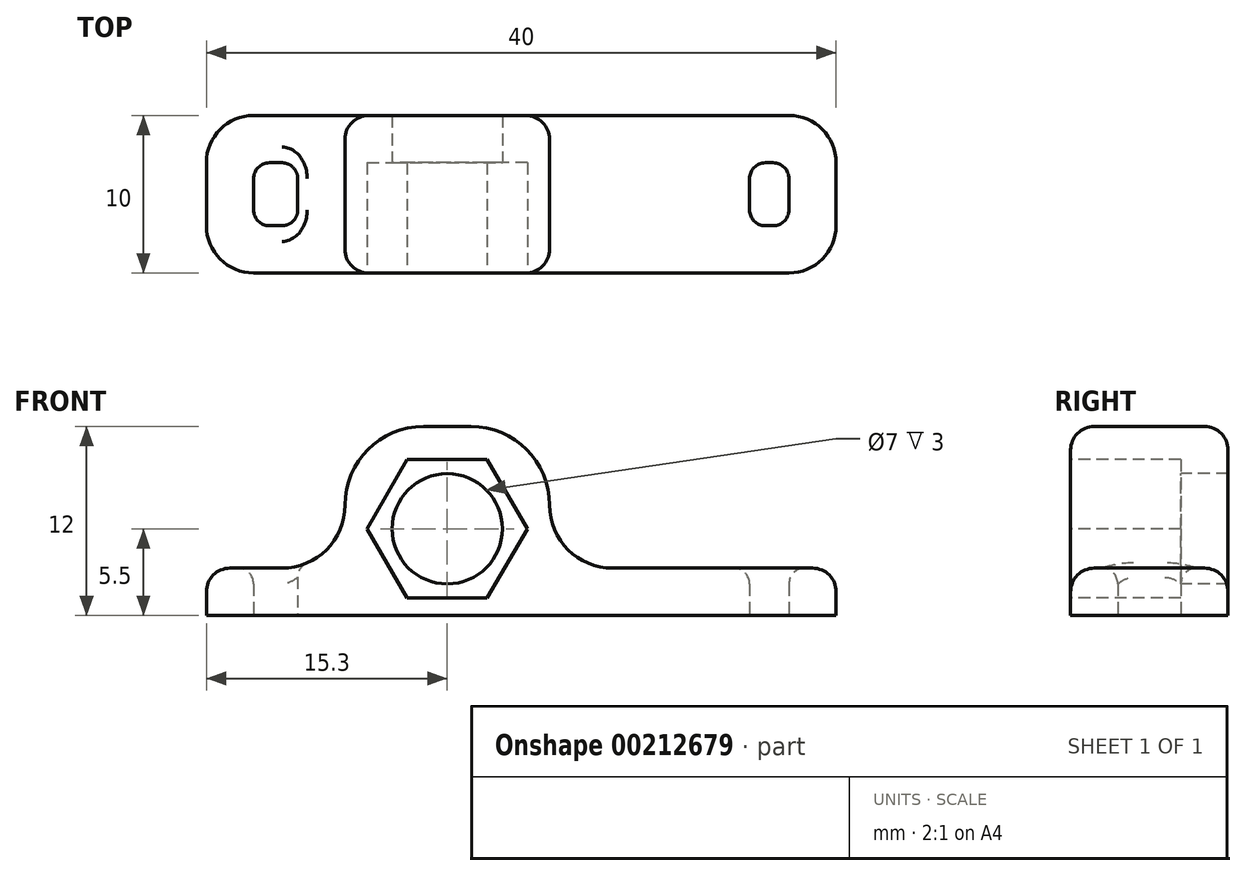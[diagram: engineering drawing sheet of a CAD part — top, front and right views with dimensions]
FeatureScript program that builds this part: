
annotation { "Feature Type Name" : "Feature", "Feature Type Description" : "" }
export const myFeature = defineFeature(function(context is Context, id is Id, definition is map)
    precondition{}
    {
        {
            var Q0;
            Q0=qCreatedBy(makeId("Top.planeOp"),FACE);
            var sketch = newSketch(context, id + "F0", { "sketchPlane" : qUnion([Q0])});
            skLineSegment(sketch, "E0.bottom", {"start": v(-17, 5) * mm, "end": v(17, 5) * mm});
            skLineSegment(sketch, "E0.top", {"start": v(-17, -5) * mm, "end": v(17, -5) * mm});
            skLineSegment(sketch, "E0.left", {"start": v(-20, 2) * mm, "end": v(-20, -2) * mm});
            skLineSegment(sketch, "E0.right", {"start": v(20, 2) * mm, "end": v(20, -2) * mm});
            skLineSegment(sketch, "E1.bottom", {"start": v(-16, 2) * mm, "end": v(-15.2, 2) * mm});
            skLineSegment(sketch, "E1.top", {"start": v(-16, -2) * mm, "end": v(-15.2, -2) * mm});
            skLineSegment(sketch, "E1.left", {"start": v(-17, 1) * mm, "end": v(-17, -1) * mm});
            skLineSegment(sketch, "E1.right", {"start": v(-14.2, 1) * mm, "end": v(-14.2, -1) * mm});
            skLineSegment(sketch, "E2.bottom", {"start": v(15.5, 2) * mm, "end": v(16, 2) * mm});
            skLineSegment(sketch, "E2.top", {"start": v(15.5, -2) * mm, "end": v(16, -2) * mm});
            skLineSegment(sketch, "E2.left", {"start": v(17, 1) * mm, "end": v(17, -1) * mm});
            skLineSegment(sketch, "E2.right", {"start": v(14.5, 1) * mm, "end": v(14.5, -1) * mm});
            skPoint(sketch, "E3.visualSharp", {"position": v(-17, 2) * mm});
            skArc(sketch, "E3.filletArc", {"start": v(-16, 2) * mm, "mid": v(-16.7, 1.7) * mm, "end": v(-17, 1) * mm});
            skPoint(sketch, "E4.visualSharp", {"position": v(-14.2, 2) * mm});
            skArc(sketch, "E4.filletArc", {"start": v(-14.2, 1) * mm, "mid": v(-14.5, 1.7) * mm, "end": v(-15.2, 2) * mm});
            skPoint(sketch, "E5.visualSharp", {"position": v(-17, -2) * mm});
            skArc(sketch, "E5.filletArc", {"start": v(-17, -1) * mm, "mid": v(-16.7, -1.7) * mm, "end": v(-16, -2) * mm});
            skPoint(sketch, "E6.visualSharp", {"position": v(-14.2, -2) * mm});
            skArc(sketch, "E6.filletArc", {"start": v(-15.2, -2) * mm, "mid": v(-14.5, -1.7) * mm, "end": v(-14.2, -1) * mm});
            skPoint(sketch, "E7.visualSharp", {"position": v(17, 2) * mm});
            skArc(sketch, "E7.filletArc", {"start": v(17, 1) * mm, "mid": v(16.7, 1.7) * mm, "end": v(16, 2) * mm});
            skPoint(sketch, "E8.visualSharp", {"position": v(14.5, 2) * mm});
            skArc(sketch, "E8.filletArc", {"start": v(15.5, 2) * mm, "mid": v(14.8, 1.7) * mm, "end": v(14.5, 1) * mm});
            skPoint(sketch, "E9.visualSharp", {"position": v(14.5, -2) * mm});
            skArc(sketch, "E9.filletArc", {"start": v(14.5, -1) * mm, "mid": v(14.8, -1.7) * mm, "end": v(15.5, -2) * mm});
            skPoint(sketch, "E10.visualSharp", {"position": v(17, -2) * mm});
            skArc(sketch, "E10.filletArc", {"start": v(16, -2) * mm, "mid": v(16.7, -1.7) * mm, "end": v(17, -1) * mm});
            skPoint(sketch, "E11.visualSharp", {"position": v(-20, 5) * mm});
            skArc(sketch, "E11.filletArc", {"start": v(-17, 5) * mm, "mid": v(-19.12, 4.12) * mm, "end": v(-20, 2) * mm});
            skPoint(sketch, "E12.visualSharp", {"position": v(-20, -5) * mm});
            skArc(sketch, "E12.filletArc", {"start": v(-20, -2) * mm, "mid": v(-19.12, -4.12) * mm, "end": v(-17, -5) * mm});
            skPoint(sketch, "E13.visualSharp", {"position": v(20, -5) * mm});
            skArc(sketch, "E13.filletArc", {"start": v(17, -5) * mm, "mid": v(19.12, -4.12) * mm, "end": v(20, -2) * mm});
            skPoint(sketch, "E14.visualSharp", {"position": v(20, 5) * mm});
            skArc(sketch, "E14.filletArc", {"start": v(20, 2) * mm, "mid": v(19.12, 4.12) * mm, "end": v(17, 5) * mm});
            skSolve(sketch);
        }
        {
            var Q0;
            Q0=makeQuery(id+"F0.imprint","IMPRINT",FACE,{"disambiguationData":[TD([[makeQuery(id+"F0.imprint","IMPRINT",EDGE,{"derivedFrom":sQuery(id+"F0.wireOp",EDGE,"E0.bottom")}),-1.0]])]});
            extrude(context, id + "F1", {"entities" : qUnion([Q0]), "depth" : 12 * mm});
        }
        {
            var Q0;
            Q0=makeQuery(id+"F1.opExtrude","SWEPT_FACE",FACE,{"disambiguationData":[OSD([sQuery(id+"F0.wireOp",EDGE,"E0.top")])]});
            var sketch = newSketch(context, id + "F2", { "sketchPlane" : qUnion([Q0])});
            skLineSegment(sketch, "E15.bottom", {"start": v(-21.2, 13) * mm, "end": v(-11.2, 13) * mm});
            skLineSegment(sketch, "E15.top", {"start": v(-21.2, 3) * mm, "end": v(-15.2, 3) * mm});
            skLineSegment(sketch, "E15.left", {"start": v(-21.2, 13) * mm, "end": v(-21.2, 3) * mm});
            skLineSegment(sketch, "E15.right", {"start": v(-11.2, 13) * mm, "end": v(-11.2, 7) * mm});
            skLineSegment(sketch, "E16.bottom", {"start": v(1.8, 13) * mm, "end": v(20.8, 13) * mm});
            skLineSegment(sketch, "E16.top", {"start": v(5.8, 3) * mm, "end": v(20.8, 3) * mm});
            skLineSegment(sketch, "E16.left", {"start": v(1.8, 13) * mm, "end": v(1.8, 7) * mm});
            skLineSegment(sketch, "E16.right", {"start": v(20.8, 13) * mm, "end": v(20.8, 3) * mm});
            skPoint(sketch, "E17.visualSharp", {"position": v(-11.2, 3) * mm});
            skArc(sketch, "E17.filletArc", {"start": v(-15.2, 3) * mm, "mid": v(-12.37, 4.17) * mm, "end": v(-11.2, 7) * mm});
            skPoint(sketch, "E18.visualSharp", {"position": v(1.8, 3) * mm});
            skArc(sketch, "E18.filletArc", {"start": v(1.8, 7) * mm, "mid": v(2.97, 4.17) * mm, "end": v(5.8, 3) * mm});
            skSolve(sketch);
        }
        {
            var Q0;
            Q0 = qSketchRegion(id + "F2", true);
            extrude(context, id + "F3", {"entities" : qUnion([Q0]), "operationType" : NewBodyOperationType.REMOVE, "endBound" : BoundingType.THROUGH_ALL, "oppositeDirection" : true, "depth" : 25 * mm});
        }
        {
            var Q0;
            Q0=makeQuery(id+"F3.boolean.opBoolean","INTERSECT",EDGE,{"derivedFrom":[makeQuery(id+"F1.opExtrude","CAP_FACE",FACE,{"disambiguationData":[OSD([sQuery(id+"F0.wireOp",EDGE,"E0.bottom"),sQuery(id+"F0.wireOp",EDGE,"E0.top"),sQuery(id+"F0.wireOp",EDGE,"E0.left"),sQuery(id+"F0.wireOp",EDGE,"E0.right"),sQuery(id+"F0.wireOp",EDGE,"E1.bottom"),sQuery(id+"F0.wireOp",EDGE,"E1.top"),sQuery(id+"F0.wireOp",EDGE,"E1.left"),sQuery(id+"F0.wireOp",EDGE,"E1.right"),sQuery(id+"F0.wireOp",EDGE,"E2.bottom"),sQuery(id+"F0.wireOp",EDGE,"E2.top"),sQuery(id+"F0.wireOp",EDGE,"E2.left"),sQuery(id+"F0.wireOp",EDGE,"E2.right"),sQuery(id+"F0.wireOp",EDGE,"E3.filletArc"),sQuery(id+"F0.wireOp",EDGE,"E4.filletArc"),sQuery(id+"F0.wireOp",EDGE,"E5.filletArc"),sQuery(id+"F0.wireOp",EDGE,"E6.filletArc"),sQuery(id+"F0.wireOp",EDGE,"E7.filletArc"),sQuery(id+"F0.wireOp",EDGE,"E8.filletArc"),sQuery(id+"F0.wireOp",EDGE,"E9.filletArc"),sQuery(id+"F0.wireOp",EDGE,"E10.filletArc"),sQuery(id+"F0.wireOp",EDGE,"E11.filletArc"),sQuery(id+"F0.wireOp",EDGE,"E12.filletArc"),sQuery(id+"F0.wireOp",EDGE,"E13.filletArc"),sQuery(id+"F0.wireOp",EDGE,"E14.filletArc")])],"isStart":false}),makeQuery(id+"F3.opExtrude","SWEPT_FACE",FACE,{"disambiguationData":[OSD([sQuery(id+"F2.wireOp",EDGE,"E15.right")])]})]});
            var Q1;
            Q1=makeQuery(id+"F3.boolean.opBoolean","INTERSECT",EDGE,{"derivedFrom":[makeQuery(id+"F1.opExtrude","CAP_FACE",FACE,{"disambiguationData":[OSD([sQuery(id+"F0.wireOp",EDGE,"E0.bottom"),sQuery(id+"F0.wireOp",EDGE,"E0.top"),sQuery(id+"F0.wireOp",EDGE,"E0.left"),sQuery(id+"F0.wireOp",EDGE,"E0.right"),sQuery(id+"F0.wireOp",EDGE,"E1.bottom"),sQuery(id+"F0.wireOp",EDGE,"E1.top"),sQuery(id+"F0.wireOp",EDGE,"E1.left"),sQuery(id+"F0.wireOp",EDGE,"E1.right"),sQuery(id+"F0.wireOp",EDGE,"E2.bottom"),sQuery(id+"F0.wireOp",EDGE,"E2.top"),sQuery(id+"F0.wireOp",EDGE,"E2.left"),sQuery(id+"F0.wireOp",EDGE,"E2.right"),sQuery(id+"F0.wireOp",EDGE,"E3.filletArc"),sQuery(id+"F0.wireOp",EDGE,"E4.filletArc"),sQuery(id+"F0.wireOp",EDGE,"E5.filletArc"),sQuery(id+"F0.wireOp",EDGE,"E6.filletArc"),sQuery(id+"F0.wireOp",EDGE,"E7.filletArc"),sQuery(id+"F0.wireOp",EDGE,"E8.filletArc"),sQuery(id+"F0.wireOp",EDGE,"E9.filletArc"),sQuery(id+"F0.wireOp",EDGE,"E10.filletArc"),sQuery(id+"F0.wireOp",EDGE,"E11.filletArc"),sQuery(id+"F0.wireOp",EDGE,"E12.filletArc"),sQuery(id+"F0.wireOp",EDGE,"E13.filletArc"),sQuery(id+"F0.wireOp",EDGE,"E14.filletArc")])],"isStart":false}),makeQuery(id+"F3.opExtrude","SWEPT_FACE",FACE,{"disambiguationData":[OSD([sQuery(id+"F2.wireOp",EDGE,"E16.left")])]})]});
            fillet(context, id + "F4", {"entities" : qUnion([Q0, Q1]), "radius" : 5 * mm, "tangentPropagation" : true, "allowEdgeOverflow" : false});
        }
        {
            var Q0;
            Q0=makeQuery(id+"F1.opExtrude","SWEPT_FACE",FACE,{"disambiguationData":[OSD([sQuery(id+"F0.wireOp",EDGE,"E0.top")])]});
            var sketch = newSketch(context, id + "F5", { "sketchPlane" : qUnion([Q0])});
            skCircle(sketch, "E19", {"center": v(-4.7, 5.5) * mm, "radius": 3.5 * mm});
            skSolve(sketch);
        }
        {
            var Q0;
            Q0=makeQuery(id+"F5.imprint","IMPRINT",FACE,{"disambiguationData":[TD([[makeQuery(id+"F5.imprint","IMPRINT",EDGE,{"derivedFrom":sQuery(id+"F5.wireOp",EDGE,"E19")}),1.0]])]});
            extrude(context, id + "F6", {"entities" : qUnion([Q0]), "operationType" : NewBodyOperationType.REMOVE, "endBound" : BoundingType.THROUGH_ALL, "oppositeDirection" : true, "depth" : 25 * mm});
        }
        {
            var Q0;
            Q0=makeQuery(id+"F1.opExtrude","SWEPT_FACE",FACE,{"disambiguationData":[OSD([sQuery(id+"F0.wireOp",EDGE,"E0.top")])]});
            var sketch = newSketch(context, id + "F7", { "sketchPlane" : qUnion([Q0])});
            skCircle(sketch, "E20.cCircle", {"center": v(-4.7, 5.5) * mm, "radius": 4.4 * mm, "construction": true});
            skLineSegment(sketch, "E20.0", {"start": v(-2.16, 1.1) * mm, "end": v(-7.24, 1.1) * mm});
            skLineSegment(sketch, "E20.1", {"start": v(-7.24, 1.1) * mm, "end": v(-9.78, 5.5) * mm});
            skLineSegment(sketch, "E20.2", {"start": v(-9.78, 5.5) * mm, "end": v(-7.24, 9.9) * mm});
            skLineSegment(sketch, "E20.3", {"start": v(-7.24, 9.9) * mm, "end": v(-2.16, 9.9) * mm});
            skLineSegment(sketch, "E20.4", {"start": v(-2.16, 9.9) * mm, "end": v(0.38, 5.5) * mm});
            skLineSegment(sketch, "E20.5", {"start": v(0.38, 5.5) * mm, "end": v(-2.16, 1.1) * mm});
            skPoint(sketch, "E20.0.midPoint", {"position": v(-4.7, 1.1) * mm});
            skSolve(sketch);
        }
        {
            var Q0;
            Q0 = qSketchRegion(id + "F7", true);
            extrude(context, id + "F8", {"entities" : qUnion([Q0]), "operationType" : NewBodyOperationType.REMOVE, "oppositeDirection" : true, "depth" : 7 * mm});
        }
        {
            var Q0;
            Q0=makeQuery(id+"F3.boolean.opBoolean","INTERSECT",EDGE,{"derivedFrom":[makeQuery(id+"F1.opExtrude","SWEPT_FACE",FACE,{"disambiguationData":[OSD([sQuery(id+"F0.wireOp",EDGE,"E0.right")])]}),makeQuery(id+"F3.opExtrude","SWEPT_FACE",FACE,{"disambiguationData":[OSD([sQuery(id+"F2.wireOp",EDGE,"E16.top")])]})]});
            fillet(context, id + "F9", {"entities" : qUnion([Q0]), "radius" : 1.5 * mm, "tangentPropagation" : true, "allowEdgeOverflow" : false});
        }
        {
            var Q0;
            Q0=makeQuery(id+"F3.boolean.opBoolean","INTERSECT",EDGE,{"derivedFrom":[makeQuery(id+"F1.opExtrude","SWEPT_FACE",FACE,{"disambiguationData":[OSD([sQuery(id+"F0.wireOp",EDGE,"E2.left")])]}),makeQuery(id+"F3.opExtrude","SWEPT_FACE",FACE,{"disambiguationData":[OSD([sQuery(id+"F2.wireOp",EDGE,"E16.top")])]})]});
            var Q1;
            Q1=makeQuery(id+"F3.boolean.opBoolean","INTERSECT",EDGE,{"derivedFrom":[makeQuery(id+"F1.opExtrude","SWEPT_FACE",FACE,{"disambiguationData":[OSD([sQuery(id+"F0.wireOp",EDGE,"E1.left")])]}),makeQuery(id+"F3.opExtrude","SWEPT_FACE",FACE,{"disambiguationData":[OSD([sQuery(id+"F2.wireOp",EDGE,"E15.top")])]})]});
            fillet(context, id + "F10", {"entities" : qUnion([Q0, Q1]), "radius" : 1 * mm, "tangentPropagation" : true, "allowEdgeOverflow" : false});
        }
    });
